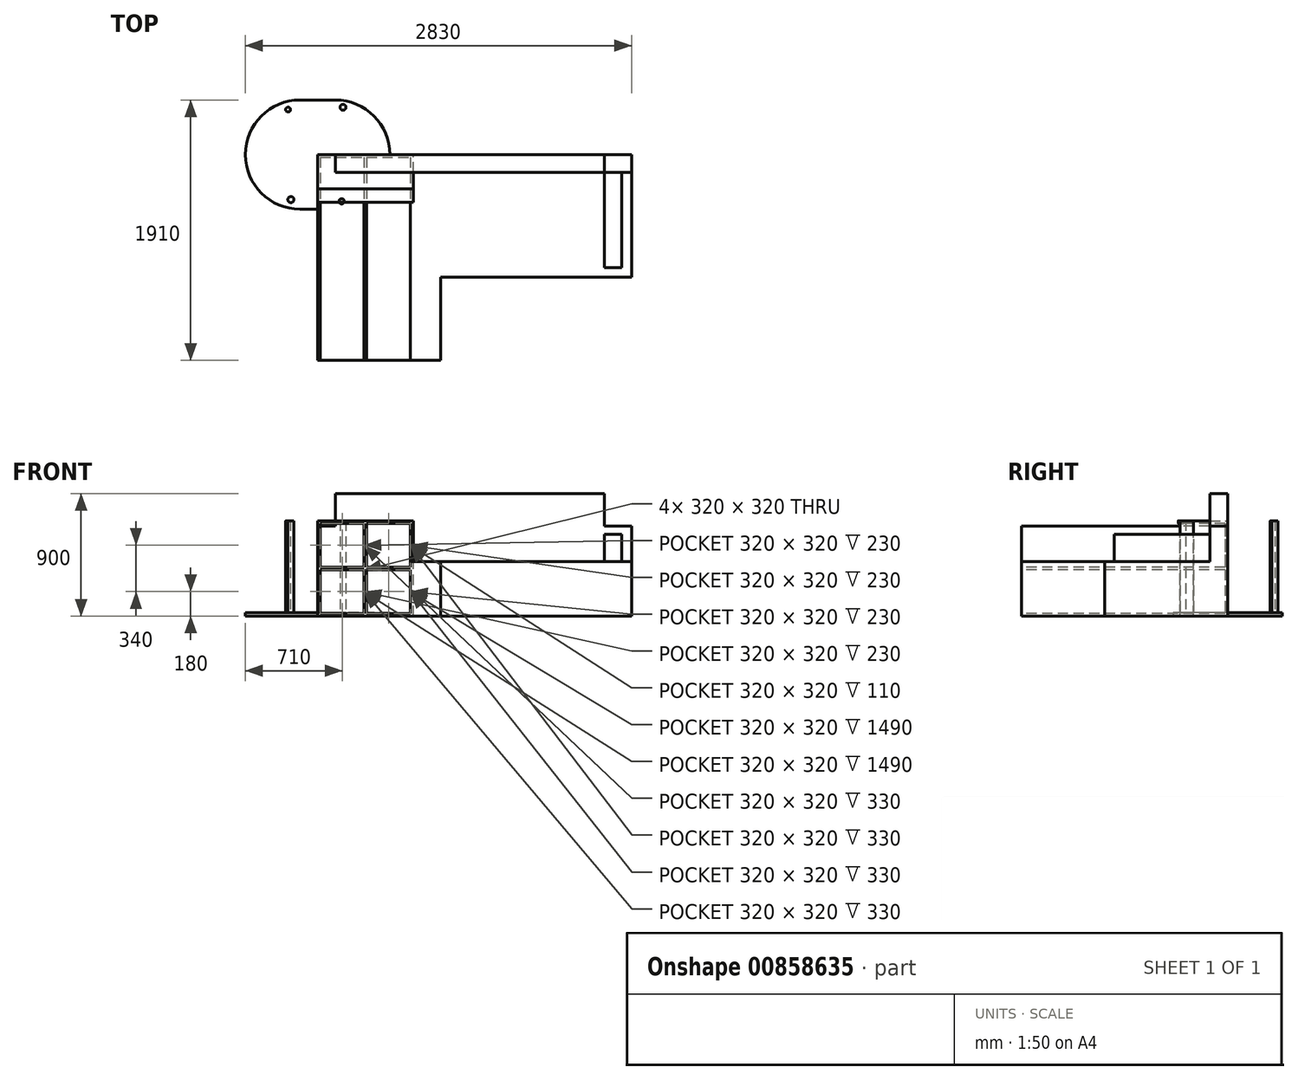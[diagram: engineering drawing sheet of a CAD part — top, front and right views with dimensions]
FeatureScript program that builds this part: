
annotation { "Feature Type Name" : "Feature", "Feature Type Description" : "" }
export const myFeature = defineFeature(function(context is Context, id is Id, definition is map)
    precondition{}
    {
        {
            var Q0;
            Q0=qCreatedBy(makeId("Top.planeOp"),FACE);
            var sketch = newSketch(context, id + "F0", { "sketchPlane" : qUnion([Q0])});
            skLineSegment(sketch, "E0", {"start": v(0, 0) * mm, "end": v(0, -1360) * mm});
            skLineSegment(sketch, "E1", {"start": v(0, -1360) * mm, "end": v(900, -1360) * mm});
            skLineSegment(sketch, "E2", {"start": v(900, -1360) * mm, "end": v(900, -830) * mm});
            skLineSegment(sketch, "E3", {"start": v(900, -830) * mm, "end": v(2230, -830) * mm});
            skLineSegment(sketch, "E4", {"start": v(2230, -830) * mm, "end": v(2230, 0) * mm});
            skLineSegment(sketch, "E5", {"start": v(2230, 0) * mm, "end": v(0, 0) * mm});
            skSolve(sketch);
        }
        {
            var Q0;
            Q0=makeQuery(id+"F0.imprint","IMPRINT",FACE,{"disambiguationData":[TD([[makeQuery(id+"F0.imprint","IMPRINT",EDGE,{"derivedFrom":sQuery(id+"F0.wireOp",EDGE,"E0")}),1.0]])]});
            extrude(context, id + "F1", {"entities" : qUnion([Q0]), "depth" : 400 * mm, "offsetDistance" : 25 * mm});
        }
        {
            var Q0;
            Q0=makeQuery(id+"F1.opExtrude","CAP_FACE",FACE,{"disambiguationData":[OSD([sQuery(id+"F0.wireOp",EDGE,"E0"),sQuery(id+"F0.wireOp",EDGE,"E1"),sQuery(id+"F0.wireOp",EDGE,"E2"),sQuery(id+"F0.wireOp",EDGE,"E3"),sQuery(id+"F0.wireOp",EDGE,"E4"),sQuery(id+"F0.wireOp",EDGE,"E5")])],"isStart":false});
            var sketch = newSketch(context, id + "F2", { "sketchPlane" : qUnion([Q0])});
            skLineSegment(sketch, "E6", {"start": v(0, -830) * mm, "end": v(130, -830) * mm});
            skLineSegment(sketch, "E7", {"start": v(130, -830) * mm, "end": v(130, -130) * mm});
            skLineSegment(sketch, "E8", {"start": v(130, -130) * mm, "end": v(2100, -130) * mm});
            skLineSegment(sketch, "E9", {"start": v(2100, -130) * mm, "end": v(2100, -830) * mm});
            skLineSegment(sketch, "E10", {"start": v(2100, -830) * mm, "end": v(2230, -830) * mm});
            skLineSegment(sketch, "E11", {"start": v(2230, -830) * mm, "end": v(2230, 0) * mm});
            skLineSegment(sketch, "E12", {"start": v(2230, 0) * mm, "end": v(0, 0) * mm});
            skLineSegment(sketch, "E13", {"start": v(0, 0) * mm, "end": v(0, -830) * mm});
            skSolve(sketch);
        }
        {
            var Q0;
            Q0=makeQuery(id+"F2.imprint","IMPRINT",FACE,{"disambiguationData":[TD([[makeQuery(id+"F2.imprint","IMPRINT",EDGE,{"derivedFrom":sQuery(id+"F2.wireOp",EDGE,"E6")}),1.0]])]});
            extrude(context, id + "F3", {"entities" : qUnion([Q0]), "operationType" : NewBodyOperationType.ADD, "depth" : 500 * mm, "offsetDistance" : 25 * mm});
        }
        {
            var Q0;
            Q0=makeQuery(id+"F3.opExtrude","CAP_FACE",FACE,{"disambiguationData":[OSD([sQuery(id+"F2.wireOp",EDGE,"E6"),sQuery(id+"F2.wireOp",EDGE,"E7"),sQuery(id+"F2.wireOp",EDGE,"E8"),sQuery(id+"F2.wireOp",EDGE,"E9"),sQuery(id+"F2.wireOp",EDGE,"E10"),sQuery(id+"F2.wireOp",EDGE,"E11"),sQuery(id+"F2.wireOp",EDGE,"E12"),sQuery(id+"F2.wireOp",EDGE,"E13")])],"isStart":false});
            var sketch = newSketch(context, id + "F4", { "sketchPlane" : qUnion([Q0])});
            skLineSegment(sketch, "E14.bottom", {"start": v(0, 0) * mm, "end": v(130, 0) * mm});
            skLineSegment(sketch, "E14.top", {"start": v(0, -830) * mm, "end": v(130, -830) * mm});
            skLineSegment(sketch, "E14.left", {"start": v(0, 0) * mm, "end": v(0, -830) * mm});
            skLineSegment(sketch, "E14.right", {"start": v(130, 0) * mm, "end": v(130, -830) * mm});
            skLineSegment(sketch, "E15.bottom", {"start": v(2230, 0) * mm, "end": v(2100, 0) * mm});
            skLineSegment(sketch, "E15.top", {"start": v(2230, -830) * mm, "end": v(2100, -830) * mm});
            skLineSegment(sketch, "E15.left", {"start": v(2230, 0) * mm, "end": v(2230, -830) * mm});
            skLineSegment(sketch, "E15.right", {"start": v(2100, 0) * mm, "end": v(2100, -830) * mm});
            skSolve(sketch);
        }
        {
            var Q0;
            {var subQ2=sQuery(id+"F4.wireOp",EDGE,"E14.bottom");Q0=makeQuery(id+"F4.imprint","IMPRINT",FACE,{"disambiguationData":[TD([[makeQuery(id+"F4.imprint","IMPRINT",EDGE,{"derivedFrom":subQ2}),1.0]])]});}
            var Q1;
            {var subQ2=sQuery(id+"F4.wireOp",EDGE,"E15.bottom");Q1=makeQuery(id+"F4.imprint","IMPRINT",FACE,{"disambiguationData":[TD([[makeQuery(id+"F4.imprint","IMPRINT",EDGE,{"derivedFrom":subQ2}),1.0]])]});}
            extrude(context, id + "F5", {"entities" : qUnion([Q0, Q1]), "operationType" : NewBodyOperationType.REMOVE, "oppositeDirection" : true, "depth" : 300 * mm, "offsetDistance" : 25 * mm});
        }
        {
            var Q0;
            Q0=qCreatedBy(makeId("Top.planeOp"),FACE);
            var sketch = newSketch(context, id + "F6", { "sketchPlane" : qUnion([Q0])});
            skLineSegment(sketch, "E16", {"start": v(0, 0) * mm, "end": v(0, -1510) * mm});
            skLineSegment(sketch, "E17", {"start": v(0, -1510) * mm, "end": v(900, -1510) * mm});
            skLineSegment(sketch, "E18", {"start": v(900, -1510) * mm, "end": v(900, -900) * mm});
            skLineSegment(sketch, "E19", {"start": v(900, -900) * mm, "end": v(2300, -900) * mm});
            skLineSegment(sketch, "E20", {"start": v(2300, -900) * mm, "end": v(2300, 0) * mm});
            skLineSegment(sketch, "E21", {"start": v(2300, 0) * mm, "end": v(0, 0) * mm});
            skSolve(sketch);
        }
        {
            var Q0;
            Q0=makeQuery(id+"F6.imprint","IMPRINT",FACE,{"disambiguationData":[TD([[makeQuery(id+"F6.imprint","IMPRINT",EDGE,{"derivedFrom":sQuery(id+"F6.wireOp",EDGE,"E16")}),1.0]])]});
            extrude(context, id + "F7", {"entities" : qUnion([Q0]), "depth" : 400 * mm, "offsetDistance" : 25 * mm});
        }
        {
            var Q0;
            Q0=makeQuery(id+"F7.opExtrude","CAP_FACE",FACE,{"disambiguationData":[OSD([sQuery(id+"F6.wireOp",EDGE,"E16"),sQuery(id+"F6.wireOp",EDGE,"E17"),sQuery(id+"F6.wireOp",EDGE,"E18"),sQuery(id+"F6.wireOp",EDGE,"E19"),sQuery(id+"F6.wireOp",EDGE,"E20"),sQuery(id+"F6.wireOp",EDGE,"E21")])],"isStart":false});
            var sketch = newSketch(context, id + "F8", { "sketchPlane" : qUnion([Q0])});
            skLineSegment(sketch, "E22", {"start": v(0, -1510) * mm, "end": v(130, -1510) * mm});
            skLineSegment(sketch, "E23", {"start": v(130, -1510) * mm, "end": v(130, -130) * mm});
            skLineSegment(sketch, "E24", {"start": v(130, -130) * mm, "end": v(2300, -130) * mm});
            skLineSegment(sketch, "E25", {"start": v(2300, -130) * mm, "end": v(2300, 0) * mm});
            skLineSegment(sketch, "E26", {"start": v(2300, 0) * mm, "end": v(0, 0) * mm});
            skLineSegment(sketch, "E27", {"start": v(0, 0) * mm, "end": v(0, -1510) * mm});
            skSolve(sketch);
        }
        {
            var Q0;
            Q0=makeQuery(id+"F8.imprint","IMPRINT",FACE,{"disambiguationData":[TD([[makeQuery(id+"F8.imprint","IMPRINT",EDGE,{"derivedFrom":sQuery(id+"F8.wireOp",EDGE,"E22")}),1.0]])]});
            extrude(context, id + "F9", {"entities" : qUnion([Q0]), "operationType" : NewBodyOperationType.ADD, "depth" : 260 * mm, "offsetDistance" : 25 * mm});
        }
        {
            var Q0;
            Q0=qCreatedBy(makeId("Top.planeOp"),FACE);
            var sketch = newSketch(context, id + "F10", { "sketchPlane" : qUnion([Q0])});
            skLineSegment(sketch, "E28.bottom", {"start": v(130, 400) * mm, "end": v(-130, 400) * mm});
            skLineSegment(sketch, "E28.top", {"start": v(130, -400) * mm, "end": v(-130, -400) * mm});
            skLineSegment(sketch, "E28.left", {"start": v(130, 400) * mm, "end": v(130, -400) * mm, "construction": true});
            skLineSegment(sketch, "E28.right", {"start": v(-130, 400) * mm, "end": v(-130, -400) * mm, "construction": true});
            skPoint(sketch, "E28.middle", {"position": v(0, 0) * mm});
            skArc(sketch, "E29", {"start": v(-130, 400) * mm, "mid": v(-530, 0) * mm, "end": v(-130, -400) * mm});
            skArc(sketch, "E30", {"start": v(130, -400) * mm, "mid": v(530, 0) * mm, "end": v(130, 400) * mm});
            skCircle(sketch, "E31", {"center": v(-196.23, -329.85) * mm, "radius": 22.3 * mm});
            skCircle(sketch, "E32", {"center": v(-216.94, 329.99) * mm, "radius": 17.86 * mm});
            skCircle(sketch, "E33", {"center": v(175.83, -342.47) * mm, "radius": 19.22 * mm});
            skCircle(sketch, "E34", {"center": v(185.85, 346.66) * mm, "radius": 21.42 * mm});
            skSolve(sketch);
        }
        {
            var Q0;
            Q0 = qSketchRegion(id + "F10", true);
            var Q1;
            Q1=makeQuery(id+"F10.imprint","IMPRINT",FACE,{"disambiguationData":[TD([[makeQuery(id+"F10.imprint","IMPRINT",EDGE,{"derivedFrom":sQuery(id+"F10.wireOp",EDGE,"E33")}),1.0]])]});
            var Q2;
            Q2=makeQuery(id+"F10.imprint","IMPRINT",FACE,{"disambiguationData":[TD([[makeQuery(id+"F10.imprint","IMPRINT",EDGE,{"derivedFrom":sQuery(id+"F10.wireOp",EDGE,"E31")}),1.0]])]});
            var Q3;
            Q3=makeQuery(id+"F10.imprint","IMPRINT",FACE,{"disambiguationData":[TD([[makeQuery(id+"F10.imprint","IMPRINT",EDGE,{"derivedFrom":sQuery(id+"F10.wireOp",EDGE,"E32")}),1.0]])]});
            var Q4;
            Q4=makeQuery(id+"F10.imprint","IMPRINT",FACE,{"disambiguationData":[TD([[makeQuery(id+"F10.imprint","IMPRINT",EDGE,{"derivedFrom":sQuery(id+"F10.wireOp",EDGE,"E34")}),1.0]])]});
            extrude(context, id + "F11", {"entities" : qUnion([Q0, Q1, Q2, Q3, Q4]), "depth" : 25 * mm, "offsetDistance" : 25 * mm});
        }
        {
            var Q0;
            Q0=makeQuery(id+"F10.imprint","IMPRINT",FACE,{"disambiguationData":[TD([[makeQuery(id+"F10.imprint","IMPRINT",EDGE,{"derivedFrom":sQuery(id+"F10.wireOp",EDGE,"E31")}),1.0]])]});
            var Q1;
            Q1=makeQuery(id+"F10.imprint","IMPRINT",FACE,{"disambiguationData":[TD([[makeQuery(id+"F10.imprint","IMPRINT",EDGE,{"derivedFrom":sQuery(id+"F10.wireOp",EDGE,"E33")}),1.0]])]});
            var Q2;
            Q2=makeQuery(id+"F10.imprint","IMPRINT",FACE,{"disambiguationData":[TD([[makeQuery(id+"F10.imprint","IMPRINT",EDGE,{"derivedFrom":sQuery(id+"F10.wireOp",EDGE,"E34")}),1.0]])]});
            var Q3;
            Q3=makeQuery(id+"F10.imprint","IMPRINT",FACE,{"disambiguationData":[TD([[makeQuery(id+"F10.imprint","IMPRINT",EDGE,{"derivedFrom":sQuery(id+"F10.wireOp",EDGE,"E32")}),1.0]])]});
            extrude(context, id + "F12", {"entities" : qUnion([Q0, Q1, Q2, Q3]), "operationType" : NewBodyOperationType.ADD, "depth" : 700 * mm, "offsetDistance" : 25 * mm});
        }
        {
            var Q0;
            Q0=qCreatedBy(makeId("Front.planeOp"),FACE);
            var sketch = newSketch(context, id + "F13", { "sketchPlane" : qUnion([Q0])});
            skLineSegment(sketch, "E35.bottom", {"start": v(0, 0) * mm, "end": v(700, 0) * mm});
            skLineSegment(sketch, "E35.top", {"start": v(0, 700) * mm, "end": v(700, 700) * mm});
            skLineSegment(sketch, "E35.left", {"start": v(0, 0) * mm, "end": v(0, 700) * mm});
            skLineSegment(sketch, "E35.right", {"start": v(700, 0) * mm, "end": v(700, 700) * mm});
            skSolve(sketch);
        }
        {
            var Q0;
            Q0 = qSketchRegion(id + "F13", true);
            extrude(context, id + "F14", {"entities" : qUnion([Q0]), "depth" : 250 * mm, "offsetDistance" : 25 * mm});
        }
        {
            var Q0;
            Q0=makeQuery(id+"F14.opExtrude","CAP_FACE",FACE,{"disambiguationData":[OSD([sQuery(id+"F13.wireOp",EDGE,"E35.bottom"),sQuery(id+"F13.wireOp",EDGE,"E35.top"),sQuery(id+"F13.wireOp",EDGE,"E35.left"),sQuery(id+"F13.wireOp",EDGE,"E35.right")])],"isStart":false});
            var sketch = newSketch(context, id + "F15", { "sketchPlane" : qUnion([Q0])});
            skLineSegment(sketch, "E36.bottom", {"start": v(20, 680) * mm, "end": v(340, 680) * mm});
            skLineSegment(sketch, "E36.top", {"start": v(20, 360) * mm, "end": v(340, 360) * mm});
            skLineSegment(sketch, "E36.left", {"start": v(20, 680) * mm, "end": v(20, 360) * mm});
            skLineSegment(sketch, "E36.right", {"start": v(340, 680) * mm, "end": v(340, 360) * mm});
            skLineSegment(sketch, "E37.bottom", {"start": v(360, 680) * mm, "end": v(680, 680) * mm});
            skLineSegment(sketch, "E37.top", {"start": v(360, 360) * mm, "end": v(680, 360) * mm});
            skLineSegment(sketch, "E37.left", {"start": v(360, 680) * mm, "end": v(360, 360) * mm});
            skLineSegment(sketch, "E37.right", {"start": v(680, 680) * mm, "end": v(680, 360) * mm});
            skLineSegment(sketch, "E38.bottom", {"start": v(360, 340) * mm, "end": v(680, 340) * mm});
            skLineSegment(sketch, "E38.top", {"start": v(360, 20) * mm, "end": v(680, 20) * mm});
            skLineSegment(sketch, "E38.left", {"start": v(360, 340) * mm, "end": v(360, 20) * mm});
            skLineSegment(sketch, "E38.right", {"start": v(680, 340) * mm, "end": v(680, 20) * mm});
            skLineSegment(sketch, "E39.bottom", {"start": v(20, 340) * mm, "end": v(340, 340) * mm});
            skLineSegment(sketch, "E39.top", {"start": v(20, 20) * mm, "end": v(340, 20) * mm});
            skLineSegment(sketch, "E39.left", {"start": v(20, 340) * mm, "end": v(20, 20) * mm});
            skLineSegment(sketch, "E39.right", {"start": v(340, 340) * mm, "end": v(340, 20) * mm});
            skSolve(sketch);
        }
        {
            var Q0;
            Q0=makeQuery(id+"F14.opExtrude","CAP_FACE",FACE,{"disambiguationData":[OSD([sQuery(id+"F13.wireOp",EDGE,"E35.bottom"),sQuery(id+"F13.wireOp",EDGE,"E35.top"),sQuery(id+"F13.wireOp",EDGE,"E35.left"),sQuery(id+"F13.wireOp",EDGE,"E35.right")])],"isStart":true});
            extrude(context, id + "F16", {"entities" : qUnion([Q0]), "oppositeDirection" : true, "depth" : 350 * mm, "offsetDistance" : 25 * mm});
        }
        {
            var Q0;
            Q0 = qSketchRegion(id + "F15", true);
            extrude(context, id + "F17", {"entities" : qUnion([Q0]), "operationType" : NewBodyOperationType.REMOVE, "oppositeDirection" : true, "depth" : 230 * mm, "offsetDistance" : 25 * mm, "hasSecondDirection" : true, "secondDirectionBound" : BoundingType.THROUGH_ALL, "secondDirectionOppositeDirection" : false, "secondDirectionDepth" : 25 * mm});
        }
    });
